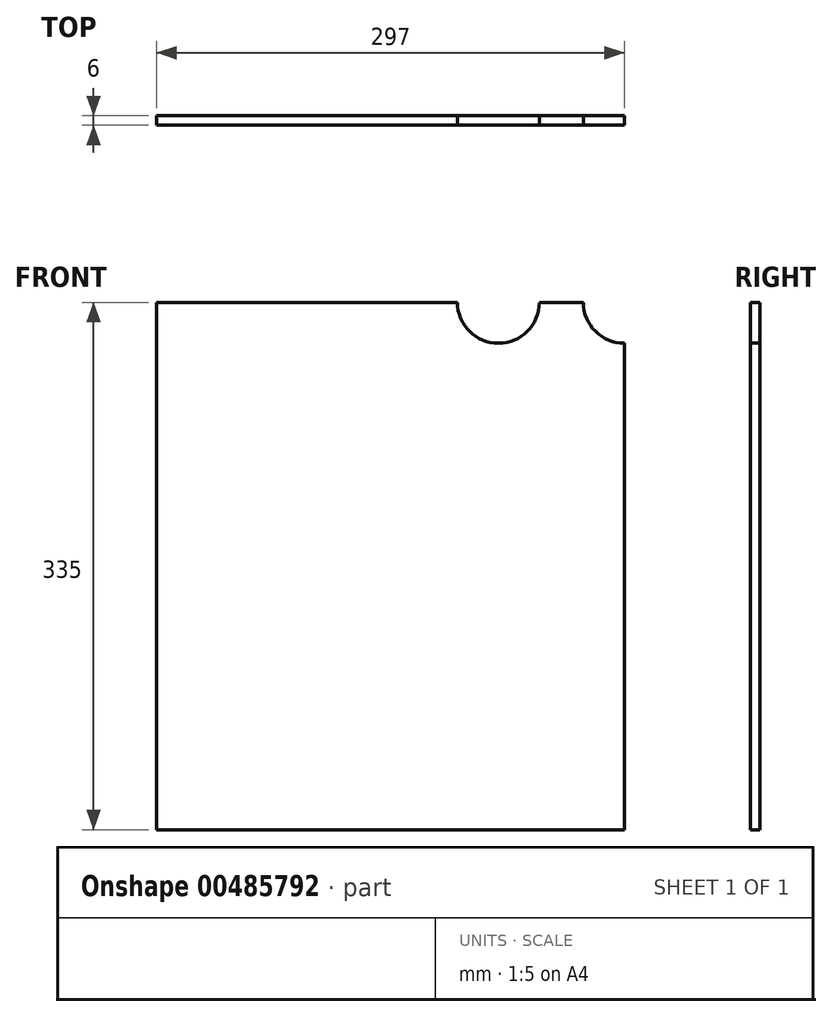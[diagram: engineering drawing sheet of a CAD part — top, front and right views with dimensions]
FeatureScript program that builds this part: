
annotation { "Feature Type Name" : "Feature", "Feature Type Description" : "" }
export const myFeature = defineFeature(function(context is Context, id is Id, definition is map)
    precondition{}
    {
        {
            var Q0;
            Q0=qCreatedBy(makeId("Front.planeOp"),FACE);
            var sketch = newSketch(context, id + "F0", { "sketchPlane" : qUnion([Q0])});
            skLineSegment(sketch, "E0.bottom", {"start": v(-575, 600) * mm, "end": v(575, 600) * mm});
            skLineSegment(sketch, "E0.top", {"start": v(-575, -600) * mm, "end": v(575, -600) * mm});
            skLineSegment(sketch, "E0.left", {"start": v(-575, 600) * mm, "end": v(-575, -600) * mm});
            skLineSegment(sketch, "E0.right", {"start": v(575, 600) * mm, "end": v(575, -600) * mm});
            skPoint(sketch, "E0.middle", {"position": v(0, 0) * mm});
            skLineSegment(sketch, "E1", {"start": v(-575, 600) * mm, "end": v(-415, 600) * mm});
            skLineSegment(sketch, "E2", {"start": v(575, -600) * mm, "end": v(575, -410) * mm});
            skLineSegment(sketch, "E3", {"start": v(575, -410) * mm, "end": v(-415, 600) * mm});
            skLineSegment(sketch, "E4.bottom", {"start": v(-575, -600) * mm, "end": v(-355, -600) * mm});
            skLineSegment(sketch, "E4.top", {"start": v(-575, -262) * mm, "end": v(-355, -262) * mm});
            skLineSegment(sketch, "E4.left", {"start": v(-575, -600) * mm, "end": v(-575, -262) * mm});
            skLineSegment(sketch, "E4.right", {"start": v(-355, -600) * mm, "end": v(-355, -262) * mm});
            skLineSegment(sketch, "E5.bottom", {"start": v(-575, -600) * mm, "end": v(-275, -600) * mm});
            skLineSegment(sketch, "E5.top", {"start": v(-575, -262) * mm, "end": v(-275, -262) * mm});
            skLineSegment(sketch, "E5.right", {"start": v(-275, -600) * mm, "end": v(-275, -262) * mm});
            skLineSegment(sketch, "E6.bottom", {"start": v(-575, -600) * mm, "end": v(-572, -600) * mm});
            skLineSegment(sketch, "E6.top", {"start": v(-575, 600) * mm, "end": v(-572, 600) * mm});
            skLineSegment(sketch, "E6.left", {"start": v(-575, -600) * mm, "end": v(-575, 600) * mm});
            skLineSegment(sketch, "E6.right", {"start": v(-572, -600) * mm, "end": v(-572, 600) * mm});
            skLineSegment(sketch, "E7.top", {"start": v(-575, -597) * mm, "end": v(575, -597) * mm});
            skLineSegment(sketch, "E7.left", {"start": v(-575, -600) * mm, "end": v(-575, -597) * mm});
            skLineSegment(sketch, "E7.right", {"start": v(575, -600) * mm, "end": v(575, -597) * mm});
            skCircle(sketch, "E8", {"center": v(-355, -262) * mm, "radius": 26 * mm});
            skCircle(sketch, "E9", {"center": v(-275, -262) * mm, "radius": 26 * mm});
            skSolve(sketch);
        }
        {
            var Q0;
            {var subQ12=sQuery(id+"F0.wireOp",EDGE,"E1");Q0=makeQuery(id+"F0.imprint","IMPRINT",FACE,{"disambiguationData":[TD([[makeQuery(id+"F0.imprint","IMPRINT",EDGE,{"derivedFrom":subQ12}),-1.0]])]});}
            var Q1;
            {var subQ0=sQuery(id+"F0.wireOp",EDGE,"E7.top");var subQ1=sQuery(id+"F0.wireOp",EDGE,"E4.right");var subQ2=makeQuery(id+"F0.imprint","INTERSECT",VERTEX,{"derivedFrom":[subQ1,subQ0]});Q1=makeQuery(id+"F0.imprint","IMPRINT",FACE,{"disambiguationData":[TD([[makeQuery(id+"F0.imprint","IMPRINT",EDGE,{"disambiguationData":[TD([[subQ2,-1.0]])],"derivedFrom":subQ1}),-1.0]])]});}
            var Q2;
            {var subQ0=sQuery(id+"F0.wireOp",EDGE,"E7.top");var subQ1=sQuery(id+"F0.wireOp",EDGE,"E4.right");var subQ2=makeQuery(id+"F0.imprint","INTERSECT",VERTEX,{"derivedFrom":[subQ1,subQ0]});Q2=makeQuery(id+"F0.imprint","IMPRINT",FACE,{"disambiguationData":[TD([[makeQuery(id+"F0.imprint","IMPRINT",EDGE,{"disambiguationData":[TD([[subQ2,-1.0]])],"derivedFrom":subQ1}),1.0]])]});}
            extrude(context, id + "F1", {"entities" : qUnion([Q0, Q1, Q2]), "depth" : 6 * mm});
        }
    });
